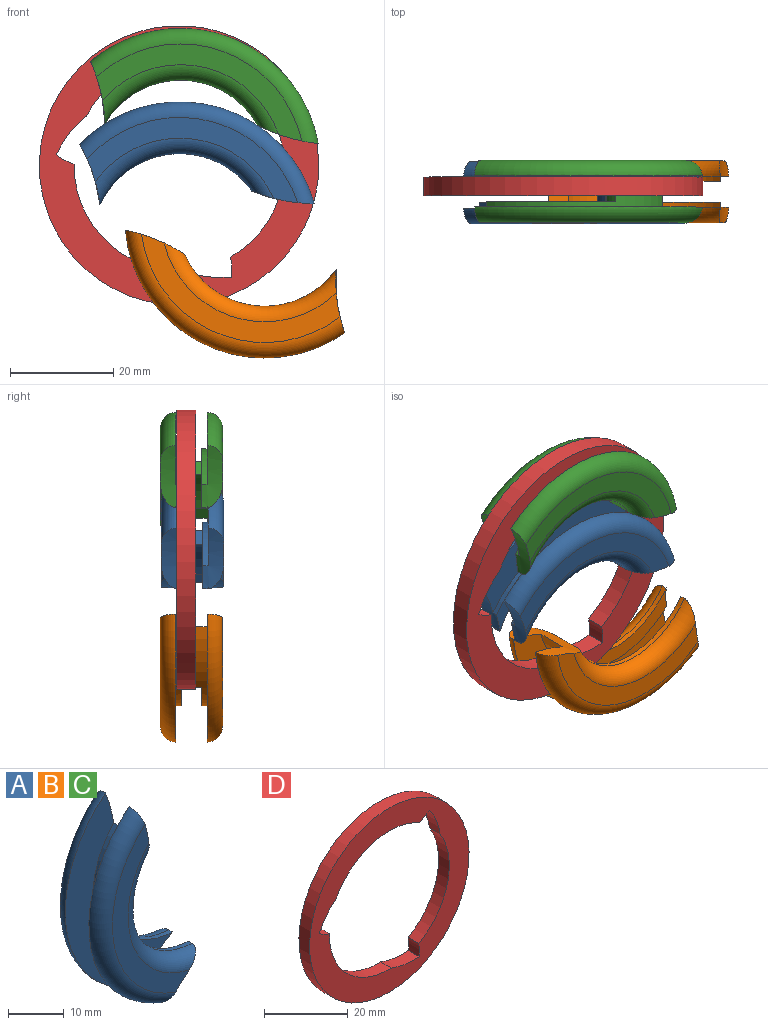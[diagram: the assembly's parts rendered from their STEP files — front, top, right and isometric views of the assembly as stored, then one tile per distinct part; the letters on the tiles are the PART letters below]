
ASSEMBLY  parts=4 mates=5
PART A: 16 faces, bbox 28.5x12x50.5 mm
  f0: cylinder r=20mm len=33.09mm, axis (0,1,0), area 142.1mm2, adj f1,f3,f4,f5,f7,f8,f9,f11
  f1: cylinder r=10mm len=4mm, axis (0,1,0), area 12.1mm2, adj f0,f2,f7,f11
  f2: cylinder r=17mm len=26.09mm, axis (0,1,0), area 109.6mm2, adj f1,f3,f5,f7,f9,f11,f12,f15
  f3: cylinder r=32mm len=12.09mm, axis (0,1,0), area 90.9mm2, adj f0,f2,f4,f6,f8,f10,f12,f13
  f4: plane 46.28x22.57mm, normal (0,-1,0), area 344.5mm2, adj f0,f3,f5,f14
  f5: cylinder r=32mm len=9.29mm, axis (0,-1,0), area 36.5mm2, adj f0,f2,f4,f6,f7,f14,f15
  f6: plane 40.84x19.57mm, normal (0,1,0), area 184.3mm2, adj f3,f5,f14,f15
  f7: plane 19.87x19.3mm, normal (0,-1,0), area 79.3mm2, adj f0,f1,f2,f5
  f8: plane 46.28x22.57mm, normal (0,1,0), area 344.5mm2, adj f0,f3,f9,f13
  f9: cylinder r=32mm len=9.29mm, axis (0,1,0), area 36.5mm2, adj f0,f2,f8,f10,f11,f12,f13
  f10: plane 40.84x19.57mm, normal (0,-1,0), area 184.3mm2, adj f3,f9,f12,f13
  f11: plane 19.87x19.3mm, normal (0,1,0), area 79.3mm2, adj f0,f1,f2,f9
  f12: torus R=20mm, axis (0,1,0), area 178.5mm2, adj f2,f3,f9,f10
  f13: torus R=24mm, axis (0,1,0), area 255.7mm2, adj f3,f8,f9,f10
  f14: torus R=24mm, axis (0,-1,0), area 255.7mm2, adj f3,f4,f5,f6
  f15: torus R=20mm, axis (0,-1,0), area 178.5mm2, adj f2,f3,f5,f6
PART B: same geometry as A
PART C: same geometry as A
PART D: 12 faces, bbox 54x3.6x54 mm
  f0: cylinder r=10.2mm len=3.6mm, axis (0,1,0), area 14mm2, adj f1,f9,f10,f11
  f1: cylinder r=20mm len=7.49mm, axis (0,1,0), area 34.4mm2, adj f0,f2,f10,f11
  f2: cylinder r=20.3mm len=28.28mm, axis (0,1,0), area 118.2mm2, adj f1,f3,f10,f11
  f3: cylinder r=10.2mm len=3.6mm, axis (0,1,0), area 14mm2, adj f2,f4,f10,f11
  f4: cylinder r=20mm len=8.77mm, axis (0,1,0), area 34.4mm2, adj f3,f5,f10,f11
  f5: cylinder r=20.3mm len=28.45mm, axis (0,1,0), area 118.2mm2, adj f4,f6,f10,f11
  f6: cylinder r=10.2mm len=3.87mm, axis (0,1,0), area 14mm2, adj f5,f7,f10,f11
  f7: cylinder r=20mm len=9.38mm, axis (0,1,0), area 34.4mm2, adj f6,f9,f10,f11
  f8: cylinder r=27mm len=54mm, axis (0,1,0), area 610.7mm2, adj f10,f11
  f9: cylinder r=20.3mm len=20.99mm, axis (0,1,0), area 118.2mm2, adj f0,f7,f10,f11
  f10: plane 54x54mm, normal (0,-1,0), area 940.2mm2, adj f0,f1,f2,f3,f4,f5,f6,f7
  f11: plane 54x54mm, normal (0,1,0), area 940.2mm2, adj f0,f1,f2,f3,f4,f5,f6,f7
PLACE A rot(axis=(0,1,0),112.5deg) t=(-49.03,-0.01,-6.8)mm
PLACE B rot(axis=(0,-1,0),56.6deg) t=(-32.63,0.19,-2.29)mm
PLACE C rot(axis=(0,1,0),118.1deg) t=(-48.86,0.19,7.4)mm
PLACE D t=(-49.17,0.19,7.92)mm fixed
MATE planar C.f4 <-> D.f8  axis (0,-1,0) through (-43.22,0.19,26.13)mm
MATE revolute C.f1 <-> D.f3  axis (0,1,0) through (-31.87,-2.81,17.96)mm
MATE planar D.f7 <-> B.f8  axis (0,-1,0) through (-41.15,-3.61,6.24)mm
MATE revolute B.f1 <-> D.f6  axis (0,1,0) through (-50.51,-2.81,-11.25)mm
MATE planar D.f8 <-> A.f4  axis (0,1,0) through (-49.17,-0.01,7.92)mm
